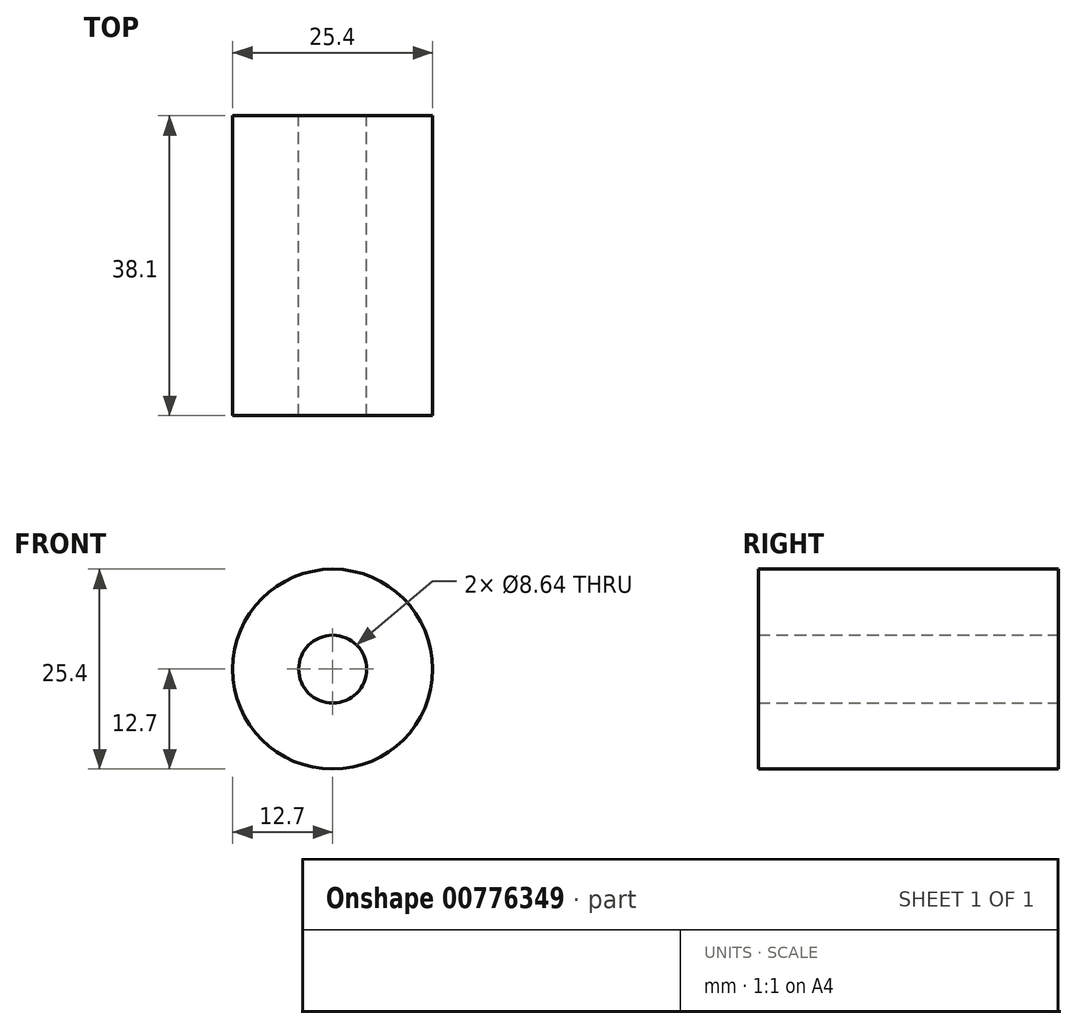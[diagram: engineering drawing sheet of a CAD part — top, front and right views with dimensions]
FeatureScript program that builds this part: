
annotation { "Feature Type Name" : "Feature", "Feature Type Description" : "" }
export const myFeature = defineFeature(function(context is Context, id is Id, definition is map)
    precondition{}
    {
        {
            var Q0;
            Q0=qCreatedBy(makeId("Front.planeOp"),FACE);
            var sketch = newSketch(context, id + "F0", { "sketchPlane" : qUnion([Q0])});
            skCircle(sketch, "E0", {"center": v(0, 0) * mm, "radius": 4.32 * mm});
            skCircle(sketch, "E1", {"center": v(0, 0) * mm, "radius": 12.7 * mm});
            skSolve(sketch);
        }
        {
            var Q0;
            Q0 = qSketchRegion(id + "F0", true);
            extrude(context, id + "F1", {"entities" : qUnion([Q0]), "depth" : 38.1 * mm, "offsetDistance" : 25.4 * mm});
        }
    });
